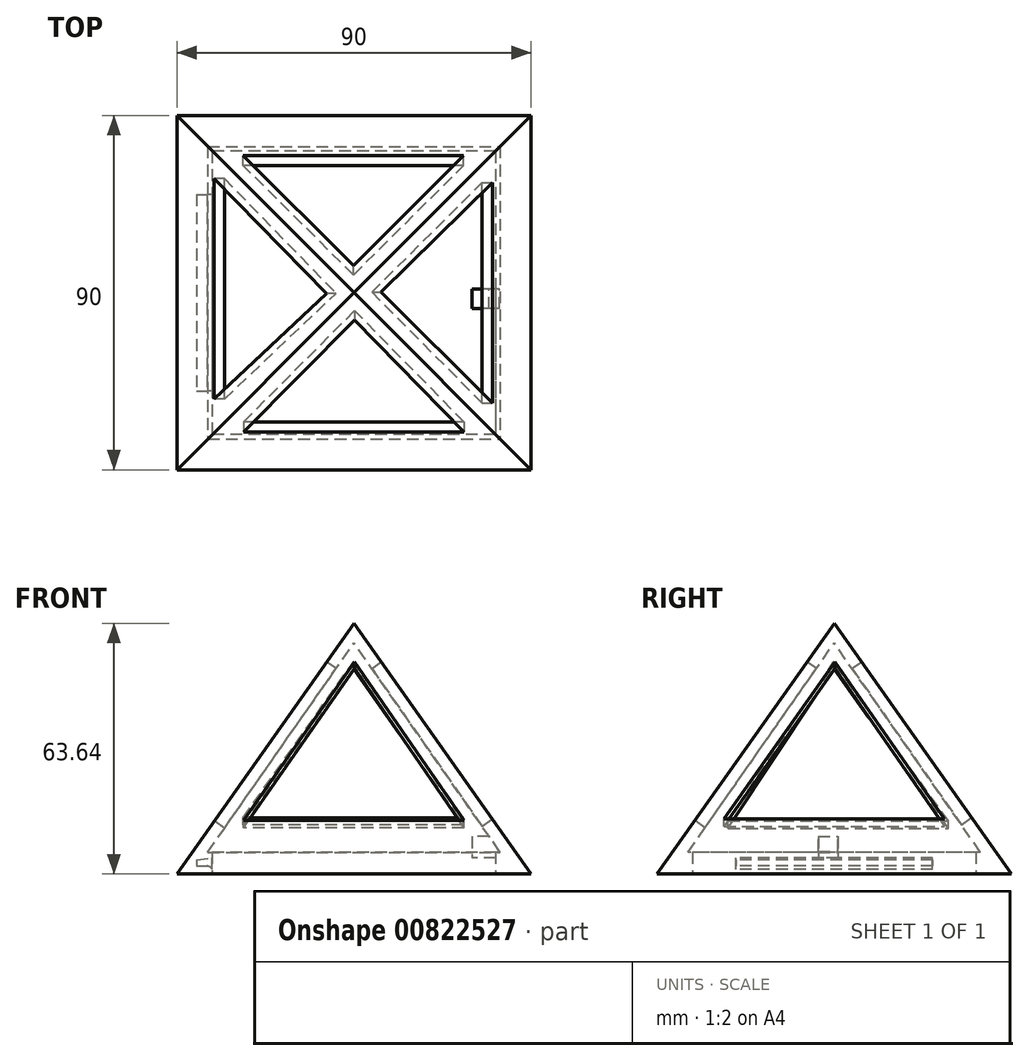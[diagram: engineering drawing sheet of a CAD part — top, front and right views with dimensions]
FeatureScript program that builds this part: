
annotation { "Feature Type Name" : "Feature", "Feature Type Description" : "" }
export const myFeature = defineFeature(function(context is Context, id is Id, definition is map)
    precondition{}
    {
        {
            var Q0;
            Q0=qCreatedBy(makeId("Top.planeOp"),FACE);
            cPlane(context, id + "F0", {"entities" : qUnion([Q0]), "cplaneType" : CPlaneType.OFFSET, "offset" : 63.64 * mm, "width" : 150 * mm, "height" : 150 * mm});
        }
        {
            var Q0;
            Q0=qCreatedBy(id+"F0.planeOp",FACE);
            var sketch = newSketch(context, id + "F1", { "sketchPlane" : qUnion([Q0])});
            skPoint(sketch, "E0", {"position": v(0, 0) * mm});
            skSolve(sketch);
        }
        {
            var Q0;
            Q0=qCreatedBy(makeId("Top.planeOp"),FACE);
            var sketch = newSketch(context, id + "F2", { "sketchPlane" : qUnion([Q0])});
            skLineSegment(sketch, "E1.bottom", {"start": v(-45, 45) * mm, "end": v(45, 45) * mm});
            skLineSegment(sketch, "E1.top", {"start": v(-45, -45) * mm, "end": v(45, -45) * mm});
            skLineSegment(sketch, "E1.left", {"start": v(-45, 45) * mm, "end": v(-45, -45) * mm});
            skLineSegment(sketch, "E1.right", {"start": v(45, 45) * mm, "end": v(45, -45) * mm});
            skPoint(sketch, "E2.orphan", {"position": v(-45, 0) * mm});
            skPoint(sketch, "E3.start.orphan", {"position": v(45, 0) * mm});
            skPoint(sketch, "E4.end.orphan", {"position": v(0, -45) * mm});
            skPoint(sketch, "E4.start.orphan", {"position": v(0, 45) * mm});
            skSolve(sketch);
        }
        {
            var Q0;
            Q0=makeQuery(id+"F2.imprint","IMPRINT",FACE,{"disambiguationData":[TD([[makeQuery(id+"F2.imprint","IMPRINT",EDGE,{"derivedFrom":sQuery(id+"F2.wireOp",EDGE,"E1.bottom")}),-1.0]])]});
            var Q1;
            Q1=sQuery(id+"F1.wireOp",VERTEX,"E0");
            loft(context, id + "F3", {"sheetProfilesArray" : [{ "sheetProfileEntities" : qUnion([Q0]) }, { "sheetProfileEntities" : qUnion([Q1]) }]});
        }
        {
            var Q0;
            Q0=qCreatedBy(makeId("Top.planeOp"),FACE);
            cPlane(context, id + "F4", {"entities" : qUnion([Q0]), "cplaneType" : CPlaneType.OFFSET, "offset" : 58.64 * mm, "width" : 150 * mm, "height" : 150 * mm});
        }
        {
            var Q0;
            Q0=qCreatedBy(id+"F4.planeOp",FACE);
            var sketch = newSketch(context, id + "F5", { "sketchPlane" : qUnion([Q0])});
            skPoint(sketch, "E5", {"position": v(0, 0) * mm});
            skSolve(sketch);
        }
        {
            var Q0;
            Q0=makeQuery(id+"F2.imprint","IMPRINT",FACE,{"disambiguationData":[TD([[makeQuery(id+"F2.imprint","IMPRINT",EDGE,{"derivedFrom":sQuery(id+"F2.wireOp",EDGE,"E1.bottom")}),-1.0]])]});
            var sketch = newSketch(context, id + "F6", { "sketchPlane" : qUnion([Q0])});
            skLineSegment(sketch, "E6.0", {"start": v(-41, 41) * mm, "end": v(-41, -41) * mm});
            skLineSegment(sketch, "E6.1", {"start": v(-41, 41) * mm, "end": v(41, 41) * mm});
            skLineSegment(sketch, "E6.2", {"start": v(41, 41) * mm, "end": v(41, -41) * mm});
            skLineSegment(sketch, "E6.3", {"start": v(-41, -41) * mm, "end": v(41, -41) * mm});
            skSolve(sketch);
        }
        {
            var Q1;
            Q1=makeQuery(id+"F6.imprint","IMPRINT",FACE,{"disambiguationData":[TD([[makeQuery(id+"F6.imprint","IMPRINT",EDGE,{"derivedFrom":sQuery(id+"F6.wireOp",EDGE,"E6.0")}),1.0]])]});
            var Q2;
            Q2=sQuery(id+"F5.wireOp",VERTEX,"E5");
            loft(context, id + "F7", {"operationType" : NewBodyOperationType.REMOVE, "sheetProfilesArray" : [{ "sheetProfileEntities" : qUnion([Q1]) }, { "sheetProfileEntities" : qUnion([Q2]) }]});
        }
        {
            var Q0;
            Q0=makeQuery(id+"F3.opLoft","SWEPT_FACE",FACE,{"disambiguationData":[OSD([sQuery(id+"F2.wireOp",EDGE,"E1.bottom"),sQuery(id+"F2.wireOp",EDGE,"E1.top"),sQuery(id+"F2.wireOp",EDGE,"E1.right")])]});
            var sketch = newSketch(context, id + "F8", { "sketchPlane" : qUnion([Q0])});
            skLineSegment(sketch, "E7.0", {"start": v(-28, -8.9) * mm, "end": v(0.15, 39.96) * mm});
            skLineSegment(sketch, "E7.1", {"start": v(27.96, -8.9) * mm, "end": v(0.15, 39.96) * mm});
            skLineSegment(sketch, "E8.0", {"start": v(27.96, -8.9) * mm, "end": v(-28, -8.9) * mm});
            skLineSegment(sketch, "E9", {"start": v(0, 51.96) * mm, "end": v(0.15, 39.96) * mm});
            skSolve(sketch);
        }
        {
            var Q0;
            Q0=makeQuery(id+"F3.opLoft","SWEPT_FACE",FACE,{"disambiguationData":[OSD([sQuery(id+"F2.wireOp",EDGE,"E1.bottom"),sQuery(id+"F2.wireOp",EDGE,"E1.left"),sQuery(id+"F2.wireOp",EDGE,"E1.right")])]});
            var sketch = newSketch(context, id + "F9", { "sketchPlane" : qUnion([Q0])});
            skLineSegment(sketch, "E10.0", {"start": v(-27.84, -8.5) * mm, "end": v(0.15, 39.96) * mm});
            skLineSegment(sketch, "E10.1", {"start": v(28.13, -8.5) * mm, "end": v(0.15, 39.96) * mm});
            skLineSegment(sketch, "E11.0", {"start": v(28.13, -8.5) * mm, "end": v(-27.84, -8.5) * mm});
            skLineSegment(sketch, "E12", {"start": v(0, 51.96) * mm, "end": v(0.15, 39.96) * mm});
            skSolve(sketch);
        }
        {
            var Q0;
            Q0=makeQuery(id+"F3.opLoft","SWEPT_FACE",FACE,{"disambiguationData":[OSD([sQuery(id+"F2.wireOp",EDGE,"E1.bottom"),sQuery(id+"F2.wireOp",EDGE,"E1.top"),sQuery(id+"F2.wireOp",EDGE,"E1.left")])]});
            var sketch = newSketch(context, id + "F10", { "sketchPlane" : qUnion([Q0])});
            skLineSegment(sketch, "E13.0", {"start": v(-28.98, -9.51) * mm, "end": v(0.15, 39.96) * mm});
            skLineSegment(sketch, "E13.1", {"start": v(26.99, -9.51) * mm, "end": v(0.15, 39.96) * mm});
            skLineSegment(sketch, "E14.0", {"start": v(26.99, -9.51) * mm, "end": v(-28.98, -9.51) * mm});
            skLineSegment(sketch, "E15", {"start": v(0, 51.96) * mm, "end": v(0.15, 39.96) * mm});
            skSolve(sketch);
        }
        {
            var Q0;
            Q0=makeQuery(id+"F3.opLoft","SWEPT_FACE",FACE,{"disambiguationData":[OSD([sQuery(id+"F2.wireOp",EDGE,"E1.top"),sQuery(id+"F2.wireOp",EDGE,"E1.left"),sQuery(id+"F2.wireOp",EDGE,"E1.right")])]});
            var sketch = newSketch(context, id + "F11", { "sketchPlane" : qUnion([Q0])});
            skLineSegment(sketch, "E16.0", {"start": v(-28.04, -9.4) * mm, "end": v(0.15, 39.96) * mm});
            skLineSegment(sketch, "E16.1", {"start": v(27.93, -9.4) * mm, "end": v(0.15, 39.96) * mm});
            skLineSegment(sketch, "E17.0", {"start": v(27.93, -9.4) * mm, "end": v(-28.04, -9.4) * mm});
            skLineSegment(sketch, "E18", {"start": v(0, 51.96) * mm, "end": v(0.15, 39.96) * mm});
            skSolve(sketch);
        }
        {
            var Q0;
            Q0=makeQuery(id+"F8.imprint","IMPRINT",FACE,{"disambiguationData":[TD([[makeQuery(id+"F8.imprint","IMPRINT",EDGE,{"derivedFrom":sQuery(id+"F8.wireOp",EDGE,"E7.0")}),-1.0]])]});
            extrude(context, id + "F12", {"entities" : qUnion([Q0]), "operationType" : NewBodyOperationType.REMOVE, "endBound" : BoundingType.SYMMETRIC, "oppositeDirection" : true, "depth" : 10 * mm, "offsetDistance" : 25 * mm});
        }
        {
            var Q0;
            Q0=makeQuery(id+"F9.imprint","IMPRINT",FACE,{"disambiguationData":[TD([[makeQuery(id+"F9.imprint","IMPRINT",EDGE,{"derivedFrom":sQuery(id+"F9.wireOp",EDGE,"E10.0")}),-1.0]])]});
            extrude(context, id + "F13", {"entities" : qUnion([Q0]), "operationType" : NewBodyOperationType.REMOVE, "oppositeDirection" : true, "depth" : 10.1 * mm, "offsetDistance" : 25 * mm});
        }
        {
            var Q0;
            Q0=makeQuery(id+"F10.imprint","IMPRINT",FACE,{"disambiguationData":[TD([[makeQuery(id+"F10.imprint","IMPRINT",EDGE,{"derivedFrom":sQuery(id+"F10.wireOp",EDGE,"E13.0")}),-1.0]])]});
            extrude(context, id + "F14", {"entities" : qUnion([Q0]), "operationType" : NewBodyOperationType.REMOVE, "oppositeDirection" : true, "depth" : 10 * mm, "offsetDistance" : 25 * mm});
        }
        {
            var Q0;
            Q0=makeQuery(id+"F11.imprint","IMPRINT",FACE,{"disambiguationData":[TD([[makeQuery(id+"F11.imprint","IMPRINT",EDGE,{"derivedFrom":sQuery(id+"F11.wireOp",EDGE,"E16.0")}),-1.0]])]});
            extrude(context, id + "F15", {"entities" : qUnion([Q0]), "operationType" : NewBodyOperationType.REMOVE, "oppositeDirection" : true, "depth" : 10 * mm, "offsetDistance" : 25 * mm});
        }
        {
            var Q0;
            Q0=makeQuery(id+"F3.opLoft","SWEPT_FACE",FACE,{"disambiguationData":[OSD([sQuery(id+"F2.wireOp",EDGE,"E1.bottom"),sQuery(id+"F2.wireOp",EDGE,"E1.top"),sQuery(id+"F2.wireOp",EDGE,"E1.left")])]});
            var sketch = newSketch(context, id + "F16", { "sketchPlane" : qUnion([Q0])});
            skLineSegment(sketch, "E19", {"start": v(-30.48, -21.2) * mm, "end": v(-27.31, -21.2) * mm});
            skLineSegment(sketch, "E20", {"start": v(-27.31, -21.2) * mm, "end": v(-24.66, -18.07) * mm});
            skLineSegment(sketch, "E21", {"start": v(-24.66, -18.07) * mm, "end": v(-26.25, -18.07) * mm});
            skLineSegment(sketch, "E22", {"start": v(-26.25, -18.07) * mm, "end": v(-28.3, -20.5) * mm});
            skLineSegment(sketch, "E23", {"start": v(-28.3, -20.5) * mm, "end": v(-28.3, -14.95) * mm});
            skLineSegment(sketch, "E24", {"start": v(-28.3, -14.95) * mm, "end": v(-29.48, -14.95) * mm});
            skLineSegment(sketch, "E25", {"start": v(-29.48, -14.95) * mm, "end": v(-29.48, -20.5) * mm});
            skLineSegment(sketch, "E26", {"start": v(-29.48, -20.5) * mm, "end": v(-31.54, -18.07) * mm});
            skLineSegment(sketch, "E27", {"start": v(-31.54, -18.07) * mm, "end": v(-33.13, -18.07) * mm});
            skLineSegment(sketch, "E28", {"start": v(-33.13, -18.07) * mm, "end": v(-30.48, -21.2) * mm});
            skLineSegment(sketch, "E29", {"start": v(-13.74, -16.13) * mm, "end": v(-13.74, -14.95) * mm});
            skLineSegment(sketch, "E30", {"start": v(-13.74, -14.95) * mm, "end": v(-23.85, -14.95) * mm});
            skLineSegment(sketch, "E31", {"start": v(-23.85, -14.95) * mm, "end": v(-23.85, -16.13) * mm});
            skLineSegment(sketch, "E32", {"start": v(-23.85, -16.13) * mm, "end": v(-13.74, -16.13) * mm});
            skLineSegment(sketch, "E33", {"start": v(-13.74, -21.2) * mm, "end": v(-13.74, -20.01) * mm});
            skLineSegment(sketch, "E34", {"start": v(-13.74, -20.01) * mm, "end": v(-23.85, -20.01) * mm});
            skLineSegment(sketch, "E35", {"start": v(-23.85, -20.01) * mm, "end": v(-23.85, -21.2) * mm});
            skLineSegment(sketch, "E36", {"start": v(-23.85, -21.2) * mm, "end": v(-13.74, -21.2) * mm});
            skLineSegment(sketch, "E37", {"start": v(-15.46, -18.66) * mm, "end": v(-15.46, -17.48) * mm});
            skLineSegment(sketch, "E38", {"start": v(-15.46, -17.48) * mm, "end": v(-22.13, -17.48) * mm});
            skLineSegment(sketch, "E39", {"start": v(-22.13, -17.48) * mm, "end": v(-22.13, -18.66) * mm});
            skLineSegment(sketch, "E40", {"start": v(-22.13, -18.66) * mm, "end": v(-15.46, -18.66) * mm});
            skLineSegment(sketch, "E41", {"start": v(-9.62, -19.72) * mm, "end": v(-11.96, -14.95) * mm});
            skLineSegment(sketch, "E42", {"start": v(-11.96, -14.95) * mm, "end": v(-13.4, -14.95) * mm});
            skLineSegment(sketch, "E43", {"start": v(-13.4, -14.95) * mm, "end": v(-10.33, -21.2) * mm});
            skLineSegment(sketch, "E44", {"start": v(-10.33, -21.2) * mm, "end": v(-8.9, -21.2) * mm});
            skLineSegment(sketch, "E45", {"start": v(-8.9, -21.2) * mm, "end": v(-6.42, -16.13) * mm});
            skLineSegment(sketch, "E46", {"start": v(-6.42, -16.13) * mm, "end": v(-5.84, -16.13) * mm});
            skLineSegment(sketch, "E47", {"start": v(-5.84, -16.13) * mm, "end": v(-5.84, -21.2) * mm});
            skLineSegment(sketch, "E48", {"start": v(-5.84, -21.2) * mm, "end": v(-4.66, -21.2) * mm});
            skLineSegment(sketch, "E49", {"start": v(-4.66, -21.2) * mm, "end": v(-4.66, -16.13) * mm});
            skLineSegment(sketch, "E50", {"start": v(-4.66, -16.13) * mm, "end": v(-3.94, -16.13) * mm});
            skLineSegment(sketch, "E51", {"start": v(-3.94, -16.13) * mm, "end": v(-3.94, -14.95) * mm});
            skLineSegment(sketch, "E52", {"start": v(-3.94, -14.95) * mm, "end": v(-7.28, -14.95) * mm});
            skLineSegment(sketch, "E53", {"start": v(-7.28, -14.95) * mm, "end": v(-9.62, -19.72) * mm});
            skLineSegment(sketch, "E54", {"start": v(2.43, -20.01) * mm, "end": v(5.3, -20.01) * mm});
            skLineSegment(sketch, "E55", {"start": v(5.3, -20.01) * mm, "end": v(5.3, -17.82) * mm});
            skLineSegment(sketch, "E56", {"start": v(2.43, -17.95) * mm, "end": v(2.43, -20.01) * mm});
            skLineSegment(sketch, "E57", {"start": v(5.3, -16.6) * mm, "end": v(5.3, -14.95) * mm});
            skLineSegment(sketch, "E58", {"start": v(5.3, -14.95) * mm, "end": v(6.48, -14.95) * mm});
            skLineSegment(sketch, "E59", {"start": v(6.48, -14.95) * mm, "end": v(6.48, -16.4) * mm});
            skLineSegment(sketch, "E60", {"start": v(10.66, -14.95) * mm, "end": v(10.66, -16.14) * mm});
            skLineSegment(sketch, "E61", {"start": v(6.48, -17.65) * mm, "end": v(6.48, -20.01) * mm});
            skLineSegment(sketch, "E62", {"start": v(6.48, -20.01) * mm, "end": v(10.66, -20.01) * mm});
            skLineSegment(sketch, "E63", {"start": v(10.66, -20.01) * mm, "end": v(10.66, -21.2) * mm});
            skLineSegment(sketch, "E64", {"start": v(10.66, -21.2) * mm, "end": v(1.25, -21.2) * mm});
            skLineSegment(sketch, "E65", {"start": v(1.25, -21.2) * mm, "end": v(1.25, -16.76) * mm});
            skLineSegment(sketch, "E66", {"start": v(1.25, -16.76) * mm, "end": v(2.43, -16.76) * mm});
            skLineSegment(sketch, "E67", {"start": v(12.92, -20.01) * mm, "end": v(14.82, -16.13) * mm});
            skLineSegment(sketch, "E68", {"start": v(14.82, -16.13) * mm, "end": v(17.48, -16.13) * mm});
            skLineSegment(sketch, "E69", {"start": v(17.48, -16.13) * mm, "end": v(19.37, -20.01) * mm});
            skLineSegment(sketch, "E70", {"start": v(19.37, -20.01) * mm, "end": v(12.92, -20.01) * mm});
            skLineSegment(sketch, "E71", {"start": v(20.26, -21.2) * mm, "end": v(20.83, -20.04) * mm});
            skLineSegment(sketch, "E72", {"start": v(20.83, -20.04) * mm, "end": v(18.33, -14.95) * mm});
            skLineSegment(sketch, "E73", {"start": v(18.33, -14.95) * mm, "end": v(13.96, -14.95) * mm});
            skLineSegment(sketch, "E74", {"start": v(13.96, -14.95) * mm, "end": v(11.5, -19.98) * mm});
            skLineSegment(sketch, "E75", {"start": v(11.5, -19.98) * mm, "end": v(12.09, -21.2) * mm});
            skLineSegment(sketch, "E76", {"start": v(12.09, -21.2) * mm, "end": v(20.26, -21.2) * mm});
            skLineSegment(sketch, "E77", {"start": v(23.56, -21.2) * mm, "end": v(28.74, -15.1) * mm});
            skLineSegment(sketch, "E78", {"start": v(28.86, -14.95) * mm, "end": v(22.22, -14.95) * mm});
            skLineSegment(sketch, "E79", {"start": v(22.22, -14.95) * mm, "end": v(21.22, -16.13) * mm});
            skLineSegment(sketch, "E80", {"start": v(21.22, -16.13) * mm, "end": v(26.26, -16.13) * mm});
            skLineSegment(sketch, "E81", {"start": v(26.26, -16.13) * mm, "end": v(21.97, -21.2) * mm});
            skLineSegment(sketch, "E82", {"start": v(21.97, -21.2) * mm, "end": v(23.56, -21.2) * mm});
            skLineSegment(sketch, "E83", {"start": v(29.92, -19) * mm, "end": v(29.92, -14.95) * mm});
            skLineSegment(sketch, "E84", {"start": v(29.92, -14.95) * mm, "end": v(28.74, -14.95) * mm});
            skLineSegment(sketch, "E85", {"start": v(28.74, -15.1) * mm, "end": v(28.74, -19) * mm});
            skLineSegment(sketch, "E86", {"start": v(28.74, -19) * mm, "end": v(29.92, -19) * mm});
            skLineSegment(sketch, "E87", {"start": v(34.22, -21.2) * mm, "end": v(34.22, -17.13) * mm});
            skLineSegment(sketch, "E88", {"start": v(34.22, -17.13) * mm, "end": v(33.04, -17.13) * mm});
            skLineSegment(sketch, "E89", {"start": v(33.04, -17.13) * mm, "end": v(33.04, -21.2) * mm});
            skLineSegment(sketch, "E90", {"start": v(33.04, -21.2) * mm, "end": v(34.22, -21.2) * mm});
            skLineSegment(sketch, "E91", {"start": v(32.07, -19) * mm, "end": v(32.07, -17.13) * mm});
            skLineSegment(sketch, "E92", {"start": v(32.07, -17.13) * mm, "end": v(30.89, -17.13) * mm});
            skLineSegment(sketch, "E93", {"start": v(30.89, -17.13) * mm, "end": v(30.89, -19) * mm});
            skLineSegment(sketch, "E94", {"start": v(30.89, -19) * mm, "end": v(32.07, -19) * mm});
            skFitSpline(sketch, "E95", {"points": [v(5.3, -17.82) * mm, v(5.1, -17.85) * mm, v(4.72, -17.9) * mm, v(4.34, -17.92) * mm, v(4.16, -17.93) * mm]});
            skFitSpline(sketch, "E96", {"points": [v(4.16, -17.93) * mm, v(4, -17.94) * mm, v(3.7, -17.95) * mm, v(3.4, -17.96) * mm, v(3.25, -17.96) * mm]});
            skFitSpline(sketch, "E97", {"points": [v(3.25, -17.96) * mm, v(3.1, -17.97) * mm, v(2.83, -17.97) * mm, v(2.56, -17.96) * mm, v(2.43, -17.95) * mm]});
            skFitSpline(sketch, "E98", {"points": [v(2.43, -16.76) * mm, v(2.56, -16.77) * mm, v(2.82, -16.78) * mm, v(3.1, -16.78) * mm, v(3.23, -16.77) * mm]});
            skFitSpline(sketch, "E99", {"points": [v(3.23, -16.77) * mm, v(3.37, -16.77) * mm, v(3.67, -16.76) * mm, v(3.98, -16.74) * mm, v(4.14, -16.73) * mm]});
            skFitSpline(sketch, "E100", {"points": [v(4.14, -16.73) * mm, v(4.33, -16.71) * mm, v(4.71, -16.68) * mm, v(5.1, -16.63) * mm, v(5.3, -16.6) * mm]});
            skFitSpline(sketch, "E101", {"points": [v(6.48, -16.4) * mm, v(6.81, -16.33) * mm, v(7.5, -16.18) * mm, v(8.18, -15.97) * mm, v(8.52, -15.86) * mm]});
            skFitSpline(sketch, "E102", {"points": [v(8.52, -15.86) * mm, v(8.88, -15.74) * mm, v(9.62, -15.48) * mm, v(10.3, -15.13) * mm, v(10.66, -14.95) * mm]});
            skFitSpline(sketch, "E103", {"points": [v(10.66, -16.14) * mm, v(10.33, -16.3) * mm, v(9.66, -16.64) * mm, v(8.96, -16.92) * mm, v(8.6, -17.05) * mm]});
            skFitSpline(sketch, "E104", {"points": [v(8.6, -17.05) * mm, v(8.25, -17.18) * mm, v(7.56, -17.42) * mm, v(6.84, -17.57) * mm, v(6.48, -17.65) * mm]});
            skSolve(sketch);
        }
        {
            var Q0;
            Q0=makeQuery(id+"F3.opLoft","CAP_FACE",FACE,{"disambiguationData":[OSD([makeQuery(id+"F2.imprint","IMPRINT",FACE,{"disambiguationData":[TD([[makeQuery(id+"F2.imprint","IMPRINT",EDGE,{"derivedFrom":sQuery(id+"F2.wireOp",EDGE,"E1.bottom")}),-1.0]])]})])],"isStart":true});
            var sketch = newSketch(context, id + "F17", { "sketchPlane" : qUnion([Q0])});
            skLineSegment(sketch, "E105.bottom", {"start": v(-41, 41) * mm, "end": v(41, 41) * mm});
            skLineSegment(sketch, "E105.top", {"start": v(-41, -41) * mm, "end": v(41, -41) * mm});
            skLineSegment(sketch, "E105.left", {"start": v(-41, 41) * mm, "end": v(-41, -41) * mm});
            skLineSegment(sketch, "E105.right", {"start": v(41, 41) * mm, "end": v(41, -41) * mm});
            skLineSegment(sketch, "E106.bottom", {"start": v(36, -36) * mm, "end": v(-36, -36) * mm});
            skLineSegment(sketch, "E106.top", {"start": v(36, 36) * mm, "end": v(-36, 36) * mm});
            skLineSegment(sketch, "E106.left", {"start": v(36, -36) * mm, "end": v(36, 36) * mm});
            skLineSegment(sketch, "E106.right", {"start": v(-36, -36) * mm, "end": v(-36, 36) * mm});
            skSolve(sketch);
        }
        {
            var Q0;
            Q0=makeQuery(id+"F17.imprint","IMPRINT",FACE,{"disambiguationData":[TD([[makeQuery(id+"F17.imprint","IMPRINT",EDGE,{"derivedFrom":sQuery(id+"F17.wireOp",EDGE,"E105.bottom")}),-1.0]])]});
            extrude(context, id + "F18", {"entities" : qUnion([Q0]), "operationType" : NewBodyOperationType.ADD, "depth" : -5.5 * mm, "offsetDistance" : 25 * mm});
        }
        {
            var Q0;
            Q0=qCreatedBy(makeId("Front.planeOp"),FACE);
            var sketch = newSketch(context, id + "F19", { "sketchPlane" : qUnion([Q0])});
            skLineSegment(sketch, "E107", {"start": v(-40.04, 2) * mm, "end": v(-36, 2) * mm});
            skLineSegment(sketch, "E108", {"start": v(-40.04, 3.5) * mm, "end": v(-40.04, 2) * mm});
            skLineSegment(sketch, "E109", {"start": v(-36, 2) * mm, "end": v(-36, 4) * mm});
            skLineSegment(sketch, "E110", {"start": v(-36, 2) * mm, "end": v(-36, 1.17) * mm});
            skFitSpline(sketch, "E111", {"points": [v(-36, 1.17) * mm, v(-36.47, 1.69) * mm, v(-37.33, 2) * mm], "startDerivative": vector(-0.67, 1.12) * mm, "endDerivative": vector(-1.92, 0.56) * mm});
            skLineSegment(sketch, "E112", {"start": v(-40.04, 3.5) * mm, "end": v(-36, 4) * mm});
            skSolve(sketch);
        }
        {
            var Q0;
            Q0 = qSketchRegion(id + "F19", true);
            extrude(context, id + "F20", {"entities" : qUnion([Q0]), "operationType" : NewBodyOperationType.REMOVE, "oppositeDirection" : true, "depth" : 25 * mm, "offsetDistance" : 25 * mm, "hasSecondDirection" : true, "secondDirectionOppositeDirection" : false, "secondDirectionDepth" : 25 * mm});
        }
        {
            var Q0;
            Q0=makeQuery(id+"F18.opExtrude","CAP_FACE",FACE,{"disambiguationData":[OSD([sQuery(id+"F17.wireOp",EDGE,"E105.bottom"),sQuery(id+"F17.wireOp",EDGE,"E105.top"),sQuery(id+"F17.wireOp",EDGE,"E105.left"),sQuery(id+"F17.wireOp",EDGE,"E105.right"),sQuery(id+"F17.wireOp",EDGE,"E106.bottom"),sQuery(id+"F17.wireOp",EDGE,"E106.top"),sQuery(id+"F17.wireOp",EDGE,"E106.left"),sQuery(id+"F17.wireOp",EDGE,"E106.right")])],"isStart":false});
            var sketch = newSketch(context, id + "F21", { "sketchPlane" : qUnion([Q0])});
            skLineSegment(sketch, "E113.bottom", {"start": v(36.98, -4.02) * mm, "end": v(29.98, -4.02) * mm});
            skLineSegment(sketch, "E113.top", {"start": v(36.98, 0.98) * mm, "end": v(29.98, 0.98) * mm});
            skLineSegment(sketch, "E113.left", {"start": v(36.98, -4.02) * mm, "end": v(36.98, 0.98) * mm});
            skLineSegment(sketch, "E113.right", {"start": v(29.98, -4.02) * mm, "end": v(29.98, 0.98) * mm});
            skSolve(sketch);
        }
        {
            var Q0;
            Q0 = qSketchRegion(id + "F21", true);
            extrude(context, id + "F22", {"entities" : qUnion([Q0]), "operationType" : NewBodyOperationType.ADD, "depth" : 4 * mm, "offsetDistance" : 25 * mm, "hasSecondDirection" : true, "secondDirectionOppositeDirection" : true, "secondDirectionDepth" : 1.5 * mm});
        }
    });
